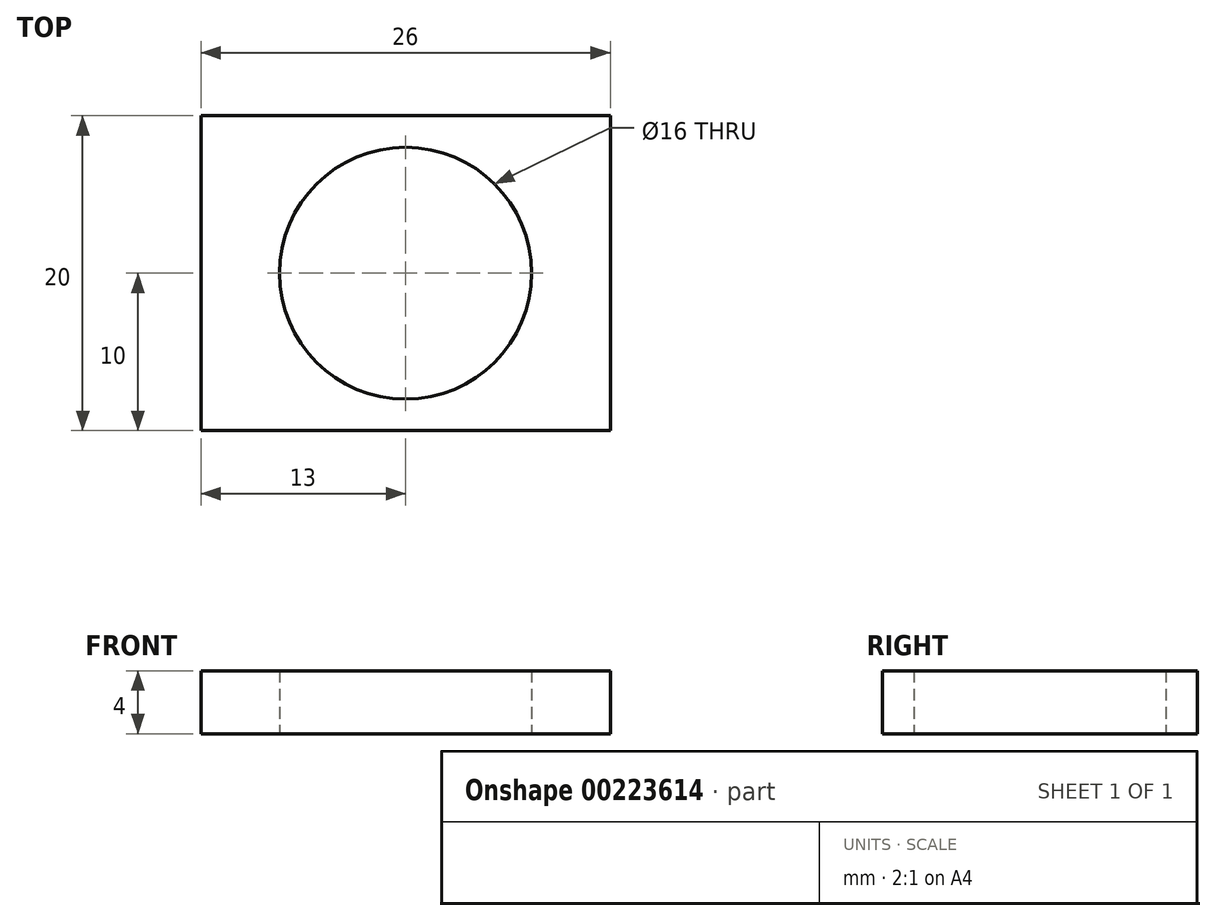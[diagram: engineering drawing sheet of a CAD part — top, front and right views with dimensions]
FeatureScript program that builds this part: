
annotation { "Feature Type Name" : "Feature", "Feature Type Description" : "" }
export const myFeature = defineFeature(function(context is Context, id is Id, definition is map)
    precondition{}
    {
        {
            var Q0;
            Q0=qCreatedBy(makeId("Top.planeOp"),FACE);
            var sketch = newSketch(context, id + "F0", { "sketchPlane" : qUnion([Q0])});
            skCircle(sketch, "E0", {"center": v(0, 0) * mm, "radius": 8 * mm});
            skLineSegment(sketch, "E1.bottom", {"start": v(-13, 10) * mm, "end": v(13, 10) * mm});
            skLineSegment(sketch, "E1.top", {"start": v(-13, -10) * mm, "end": v(13, -10) * mm});
            skLineSegment(sketch, "E1.left", {"start": v(-13, 10) * mm, "end": v(-13, -10) * mm});
            skLineSegment(sketch, "E1.right", {"start": v(13, 10) * mm, "end": v(13, -10) * mm});
            skSolve(sketch);
        }
        {
            var Q0;
            Q0=makeQuery(id+"F0.imprint","IMPRINT",FACE,{"disambiguationData":[TD([[makeQuery(id+"F0.imprint","IMPRINT",EDGE,{"derivedFrom":sQuery(id+"F0.wireOp",EDGE,"E0")}),-1.0]])]});
            extrude(context, id + "F1", {"entities" : qUnion([Q0]), "depth" : 4 * mm});
        }
    });
